AUTODESK INVENTOR PART (.ipt)
format: ipt  version: 2022 (Build 260153070, 153G)  size: 111,616 bytes
history: native  units: mm
features: other x2, extrude x2, sketch x2, shell x1
ambient origin geometry x8: Origin, YZ Plane, XZ Plane, XY Plane, X Axis, Y Axis, Z Axis, Center Point
bodies: Body1 (feature_tree)
feature tree (7):
  other  "Твердое тело1"
  extrude  "Выдавливание1"  Depth=73.0mm
  other  "НаклГрань1"
  shell  "Оболочка1"  Thickness=15.0mm
  extrude  "Выдавливание2"  Depth=0.785398mm
  sketch  "Эскиз2"
  sketch  "Эскиз3"
